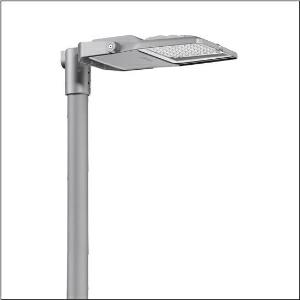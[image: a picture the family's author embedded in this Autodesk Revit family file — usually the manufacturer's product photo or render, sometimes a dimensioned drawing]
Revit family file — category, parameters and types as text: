
# Revit family: floodlight_fl_21_iq_mini___pl33t_5xa7772b4f3a_8cfb
name_source: partatom
category: Lighting Fixtures
units: mm (PartAtom-declared; Revit-internal decimal feet)

## family parameters
Cut with Voids When Loaded = No
Host = Face
Light Source = No
Part Type = Normal
Room Calculation Point = No
Round Connector Dimension = Use Diameter
Shared = No

## types (1)
- --- (1 x LED, 6420 lm, 45.5 W, 4000K)
    Apparent Load = 46 VA
    CIE Flux Codes = 26 75 99 100 100
    Color Rendering = 70
    Color Temperature = 4000K
    Default Elevation = 1800 mm
    Description = Floodlight FL 21 iQ mini, floodlight, primary light control with lens, of PMMA, primary optical cover: protective disc, of toughened safety glass, transparent, light distribution: PL33T, light emission: direct distribution, installation type: surface-mounted, LED, High Power LED, rated luminous flux: 6.420lm, luminous efficacy: 141lm/W, light colour: 740, colour temperature: 4000K, control: Auto-Match, Temp-Guard, Night-Set, Smart-Wire, Desk-Remote (wireless, voltage-free reading and setting of iQ features in the workshop via application-optimized NFC function/RFID function), optimised constant luminous flux control (CLO 2.0), Light-Fading, Lumen-Switch, with terminal, 6-pole, mains connection: 220..240V, AC, 50/60Hz, start of lifetime: 46W, end of service life: 48W, reduction: 22W, luminaire housing, of diecast aluminium, powder-coated, Siteco® metallic grey (DB 702S), corrosivity category C5 mid according to DIN EN ISO 12944, sealing non-destructively replaceable, please order mast flange separately, mast bracket, of steel, galvanised, powder-coated, protection rating (complete): IP66, insulation class (complete): insulation class II (safety insulation), certification: CE, ENEC, VDE, protection symbol: D, impact resistance: IK08, permissible operating ambient temperature: -40..+40°C, permissible operating ambient temperature for outdoor applications: -40..+50°C, standard: DIN EN 12944, LABS conformity tested according to VDMA 24364:2018-05, packaging unit: 1 piece

Light Distribution: PL33T
    Height = 70 mm
    Lamp = 1 x LED
    Lamp Light Flux = 6420 lm
    Lamp Power = 45.5 W
    Lamp count = 1
    Length = 485 mm
    Luminous efficacy = 141 lm/W
    Manufacturer = Siteco
    ModVariant = No
    Model = 5XA7772B4F3A
    Number of Poles = 1
    OnlyDefault = Yes
    Power Factor = 1
    Product Name = Floodlight FL 21 iQ mini | PL33T
    Product group = floodlight | pylon annexe
    ProductGroupID = 6200
    Protection Class = Protection class II
    Protection Degree = IP 66
    RLX_Detail_Level = 1
    RLX_Emergency_Light_Flux = 0 lm
    RLX_Emergency_Type = 0
    RLX_Emergency_Type_DB = No
    RlxData = <blob elided: 101073 chars, md5=5db0bbc9>
    Socket = socket
    Standby Power = 0 W
    System Light Flux = 6420 lm
    System Power = 46 W
    Type Comments = factory setting: luminous flux: 100 % | dim-lin: 254 | 463 mA
    Type Image = l_1007125.jpg
    URL = http://relux.com
    VarID = @adj_100045
    Voltage = 0 V
    Weight = 0.00 kg
    Width = 337 mm

## geometry (parser evidence)
native form markers: Blend x4, Sweep x13
no freeform markers — native parametric forms only
